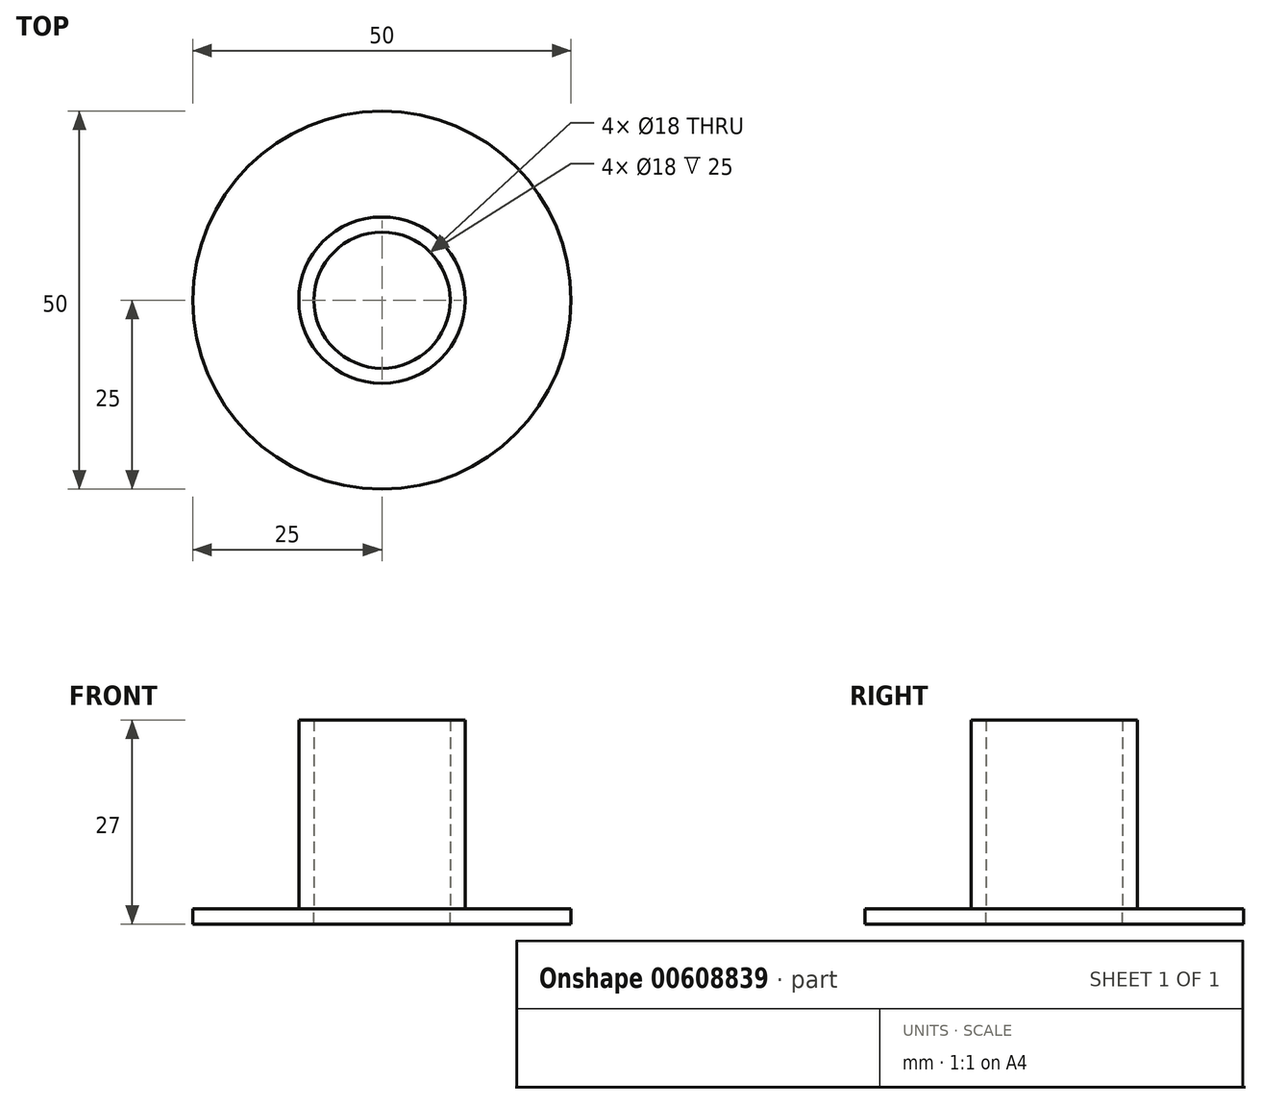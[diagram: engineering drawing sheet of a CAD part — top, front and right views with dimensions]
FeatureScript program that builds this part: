
annotation { "Feature Type Name" : "Feature", "Feature Type Description" : "" }
export const myFeature = defineFeature(function(context is Context, id is Id, definition is map)
    precondition{}
    {
        {
            var Q0;
            Q0=qCreatedBy(makeId("Top.planeOp"),FACE);
            var sketch = newSketch(context, id + "F0", { "sketchPlane" : qUnion([Q0])});
            skCircle(sketch, "E0", {"center": v(0, 0) * mm, "radius": 25 * mm});
            skSolve(sketch);
        }
        {
            var Q0;
            Q0 = qSketchRegion(id + "F0", true);
            extrude(context, id + "F1", {"entities" : qUnion([Q0]), "oppositeDirection" : true, "depth" : 2 * mm, "offsetDistance" : 25 * mm});
        }
        {
            var Q0;
            Q0=qCreatedBy(makeId("Top.planeOp"),FACE);
            var sketch = newSketch(context, id + "F2", { "sketchPlane" : qUnion([Q0])});
            skCircle(sketch, "E1", {"center": v(0, 0) * mm, "radius": 9 * mm});
            skSolve(sketch);
        }
        {
            var Q0;
            Q0 = qSketchRegion(id + "F2", true);
            extrude(context, id + "F3", {"entities" : qUnion([Q0]), "operationType" : NewBodyOperationType.REMOVE, "oppositeDirection" : true, "depth" : 25 * mm, "offsetDistance" : 25 * mm});
        }
        {
            var Q0;
            Q0=qCreatedBy(makeId("Top.planeOp"),FACE);
            var sketch = newSketch(context, id + "F4", { "sketchPlane" : qUnion([Q0])});
            skCircle(sketch, "E2", {"center": v(0, 0) * mm, "radius": 9 * mm});
            skCircle(sketch, "E3.0", {"center": v(0, 0) * mm, "radius": 11 * mm});
            skSolve(sketch);
        }
        {
            var Q0;
            Q0=makeQuery(id+"F4.imprint","IMPRINT",FACE,{"disambiguationData":[TD([[makeQuery(id+"F4.imprint","IMPRINT",EDGE,{"derivedFrom":sQuery(id+"F4.wireOp",EDGE,"E2")}),-1.0]])]});
            var Q1;
            Q1=sQuery(id+"F4.wireOp",EDGE,"E3.0");
            var Q2;
            Q2=sQuery(id+"F4.wireOp",EDGE,"E2");
            extrude(context, id + "F5", {"entities" : qUnion([Q0]), "surfaceEntities" : qUnion([Q1, Q2]), "depth" : 25 * mm, "offsetDistance" : 25 * mm});
        }
    });
